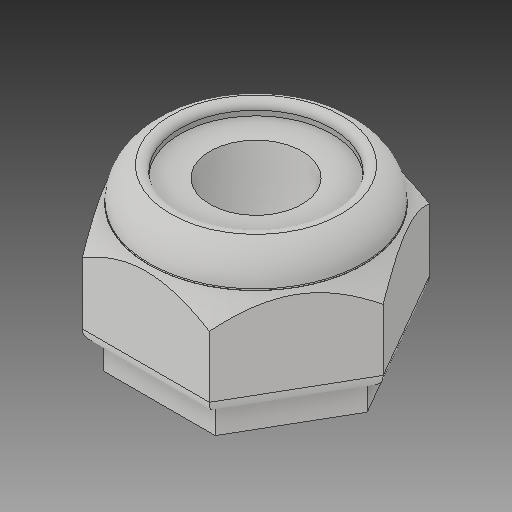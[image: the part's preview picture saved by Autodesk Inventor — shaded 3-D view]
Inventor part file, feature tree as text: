
AUTODESK INVENTOR PART (.ipt)
format: ipt  version: 2017 (Build 210142000, 142)  size: 168,448 bytes
history: native  units: in
note: dims shown in document units (in); Inventor stores cm internally (conversion verified against a paired STEP export)
features: extrude x1
ambient origin geometry x8: Origin, YZ Plane, XZ Plane, XY Plane, X Axis, Y Axis, Z Axis, Center Point
bodies: Solid1 (feature_tree)
feature tree (1):
  extrude  "Extrude1"  [1 undecoded]
note: 1 required parameter value undecoded (feature->parameter linkage not recoverable at this tier; creation-order binding heuristic only, values carry confidence <= 0.55)
